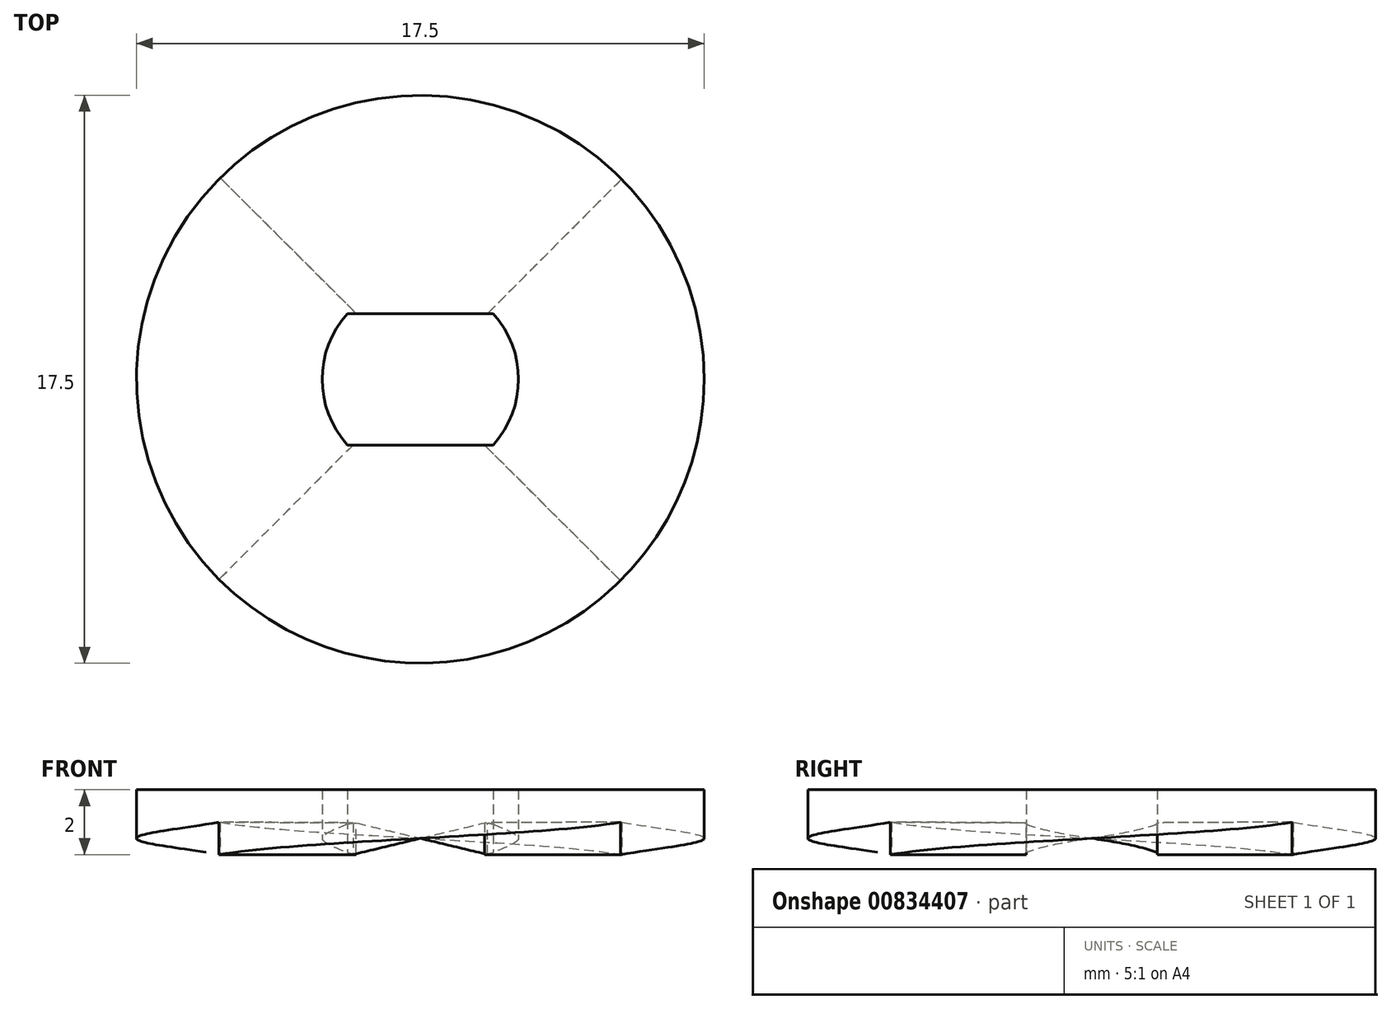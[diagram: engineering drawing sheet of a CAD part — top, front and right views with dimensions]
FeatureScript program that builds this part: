
annotation { "Feature Type Name" : "Feature", "Feature Type Description" : "" }
export const myFeature = defineFeature(function(context is Context, id is Id, definition is map)
    precondition{}
    {
        {
            var Q0;
            Q0=qCreatedBy(makeId("Front.planeOp"),FACE);
            var sketch = newSketch(context, id + "F0", { "sketchPlane" : qUnion([Q0])});
            skLineSegment(sketch, "E0", {"start": v(-0.05, 0) * mm, "end": v(0.05, 1) * mm});
            skLineSegment(sketch, "E1", {"start": v(0.05, 1) * mm, "end": v(0.05, 2) * mm});
            skLineSegment(sketch, "E2", {"start": v(0.05, 2) * mm, "end": v(-0.05, 2) * mm});
            skLineSegment(sketch, "E3", {"start": v(-0.05, 2) * mm, "end": v(-0.05, 0) * mm});
            skLineSegment(sketch, "E4", {"start": v(0, 13.58) * mm, "end": v(0, 25.88) * mm});
            skSolve(sketch);
        }
        {
            var Q0;
            Q0=qCreatedBy(makeId("Front.planeOp"),FACE);
            cPlane(context, id + "F1", {"entities" : qUnion([Q0]), "cplaneType" : CPlaneType.OFFSET, "offset" : 20 * mm, "width" : 150 * mm, "height" : 150 * mm});
        }
        {
            var Q0;
            Q0=qCreatedBy(id+"F1.planeOp",FACE);
            var sketch = newSketch(context, id + "F2", { "sketchPlane" : qUnion([Q0])});
            skLineSegment(sketch, "E5", {"start": v(-20, 0) * mm, "end": v(20, 1) * mm});
            skLineSegment(sketch, "E6", {"start": v(20, 1) * mm, "end": v(20, 2) * mm});
            skLineSegment(sketch, "E7", {"start": v(20, 2) * mm, "end": v(-20, 2) * mm});
            skLineSegment(sketch, "E8", {"start": v(-20, 2) * mm, "end": v(-20, 0) * mm});
            skSolve(sketch);
        }
        {
            var Q0;
            Q0=makeQuery(id+"F0.imprint","IMPRINT",FACE,{"disambiguationData":[TD([[makeQuery(id+"F0.imprint","IMPRINT",EDGE,{"derivedFrom":sQuery(id+"F0.wireOp",EDGE,"E0")}),1.0]])]});
            var Q1;
            Q1=makeQuery(id+"F2.imprint","IMPRINT",FACE,{"disambiguationData":[TD([[makeQuery(id+"F2.imprint","IMPRINT",EDGE,{"derivedFrom":sQuery(id+"F2.wireOp",EDGE,"E5")}),1.0]])]});
            loft(context, id + "F3", {"sheetProfilesArray" : [{ "sheetProfileEntities" : qUnion([Q0]) }, { "sheetProfileEntities" : qUnion([Q1]) }]});
        }
        {
            var Q0;
            Q0=makeQuery(id+"F3.opLoft","SWEPT_BODY",BODY,{"disambiguationData":[OSD([makeQuery(id+"F0.imprint","IMPRINT",FACE,{"disambiguationData":[TD([[makeQuery(id+"F0.imprint","IMPRINT",EDGE,{"derivedFrom":sQuery(id+"F0.wireOp",EDGE,"E0")}),1.0]])]}),makeQuery(id+"F2.imprint","IMPRINT",FACE,{"disambiguationData":[TD([[makeQuery(id+"F2.imprint","IMPRINT",EDGE,{"derivedFrom":sQuery(id+"F2.wireOp",EDGE,"E5")}),1.0]])]})])]});
            var Q1;
            Q1=sQuery(id+"F0.wireOp",EDGE,"E4");
            circularPattern(context, id + "F4", {"operationType" : NewBodyOperationType.ADD, "entities" : qUnion([Q0]), "axis" : qUnion([Q1]), "angle" : 360 * degree, "instanceCount" : 4, "equalSpace" : true});
        }
        {
            var Q0;
            Q0=qCreatedBy(makeId("Top.planeOp"),FACE);
            var sketch = newSketch(context, id + "F5", { "sketchPlane" : qUnion([Q0])});
            skCircle(sketch, "E9", {"center": v(0, 0) * mm, "radius": 8.75 * mm});
            skLineSegment(sketch, "E10.bottom", {"start": v(3.02, 2.02) * mm, "end": v(-3.02, 2.02) * mm});
            skLineSegment(sketch, "E10.top", {"start": v(3.02, -2.02) * mm, "end": v(-3.02, -2.02) * mm});
            skLineSegment(sketch, "E10.left", {"start": v(3.02, 2.02) * mm, "end": v(3.02, -2.02) * mm});
            skLineSegment(sketch, "E10.right", {"start": v(-3.02, 2.02) * mm, "end": v(-3.02, -2.02) * mm});
            skCircle(sketch, "E11", {"center": v(0, 0) * mm, "radius": 3.02 * mm});
            skCircle(sketch, "E12", {"center": v(0, 0) * mm, "radius": 3.02 * mm, "construction": true});
            skSolve(sketch);
        }
        {
            var Q0;
            Q0=makeQuery(id+"F5.imprint","IMPRINT",FACE,{"disambiguationData":[TD([[makeQuery(id+"F5.imprint","IMPRINT",EDGE,{"derivedFrom":sQuery(id+"F5.wireOp",EDGE,"E9")}),1.0]])]});
            var Q1;
            {var subQ0=sQuery(id+"F5.wireOp",EDGE,"E11");var subQ1=sQuery(id+"F5.wireOp",EDGE,"E10.left");var subQ2=makeQuery(id+"F5.imprint","INTERSECT",VERTEX,{"disambiguationData":[OD(0.0)],"derivedFrom":[subQ1,subQ0]});Q1=makeQuery(id+"F5.imprint","IMPRINT",FACE,{"disambiguationData":[TD([[makeQuery(id+"F5.imprint","IMPRINT",EDGE,{"disambiguationData":[TD([[subQ2,-1.0]])],"derivedFrom":subQ1}),1.0]])]});}
            var Q2;
            {var subQ0=sQuery(id+"F5.wireOp",EDGE,"E10.left");var subQ1=sQuery(id+"F5.wireOp",EDGE,"E10.bottom");var subQ2=makeQuery(id+"F5.imprint","INTERSECT",VERTEX,{"derivedFrom":[subQ1,subQ0]});Q2=makeQuery(id+"F5.imprint","IMPRINT",FACE,{"disambiguationData":[TD([[makeQuery(id+"F5.imprint","IMPRINT",EDGE,{"disambiguationData":[TD([[subQ2,-1.0]])],"derivedFrom":subQ1}),1.0]])]});}
            var Q3;
            {var subQ0=sQuery(id+"F5.wireOp",EDGE,"E10.right");var subQ1=sQuery(id+"F5.wireOp",EDGE,"E10.bottom");var subQ2=makeQuery(id+"F5.imprint","INTERSECT",VERTEX,{"derivedFrom":[subQ1,subQ0]});Q3=makeQuery(id+"F5.imprint","IMPRINT",FACE,{"disambiguationData":[TD([[makeQuery(id+"F5.imprint","IMPRINT",EDGE,{"disambiguationData":[TD([[subQ2,1.0]])],"derivedFrom":subQ1}),1.0]])]});}
            var Q4;
            {var subQ0=sQuery(id+"F5.wireOp",EDGE,"E11");var subQ1=sQuery(id+"F5.wireOp",EDGE,"E10.right");var subQ2=makeQuery(id+"F5.imprint","INTERSECT",VERTEX,{"disambiguationData":[OD(0.0)],"derivedFrom":[subQ1,subQ0]});Q4=makeQuery(id+"F5.imprint","IMPRINT",FACE,{"disambiguationData":[TD([[makeQuery(id+"F5.imprint","IMPRINT",EDGE,{"disambiguationData":[TD([[subQ2,-1.0]])],"derivedFrom":subQ1}),-1.0]])]});}
            var Q5;
            {var subQ0=sQuery(id+"F5.wireOp",EDGE,"E10.right");var subQ1=sQuery(id+"F5.wireOp",EDGE,"E10.top");var subQ2=makeQuery(id+"F5.imprint","INTERSECT",VERTEX,{"derivedFrom":[subQ1,subQ0]});Q5=makeQuery(id+"F5.imprint","IMPRINT",FACE,{"disambiguationData":[TD([[makeQuery(id+"F5.imprint","IMPRINT",EDGE,{"disambiguationData":[TD([[subQ2,1.0]])],"derivedFrom":subQ1}),-1.0]])]});}
            var Q6;
            {var subQ0=sQuery(id+"F5.wireOp",EDGE,"E10.left");var subQ1=sQuery(id+"F5.wireOp",EDGE,"E10.top");var subQ2=makeQuery(id+"F5.imprint","INTERSECT",VERTEX,{"derivedFrom":[subQ1,subQ0]});Q6=makeQuery(id+"F5.imprint","IMPRINT",FACE,{"disambiguationData":[TD([[makeQuery(id+"F5.imprint","IMPRINT",EDGE,{"disambiguationData":[TD([[subQ2,-1.0]])],"derivedFrom":subQ1}),-1.0]])]});}
            var Q7;
            {var subQ0=sQuery(id+"F5.wireOp",EDGE,"E11");var subQ1=sQuery(id+"F5.wireOp",EDGE,"E10.top");var subQ2=makeQuery(id+"F5.imprint","INTERSECT",VERTEX,{"disambiguationData":[OD(0.0)],"derivedFrom":[subQ1,subQ0]});Q7=makeQuery(id+"F5.imprint","IMPRINT",FACE,{"disambiguationData":[TD([[makeQuery(id+"F5.imprint","IMPRINT",EDGE,{"disambiguationData":[TD([[subQ2,-1.0]])],"derivedFrom":subQ1}),1.0]])]});}
            var Q8;
            {var subQ0=sQuery(id+"F5.wireOp",EDGE,"E11");var subQ1=sQuery(id+"F5.wireOp",EDGE,"E10.bottom");var subQ2=makeQuery(id+"F5.imprint","INTERSECT",VERTEX,{"disambiguationData":[OD(0.0)],"derivedFrom":[subQ1,subQ0]});Q8=makeQuery(id+"F5.imprint","IMPRINT",FACE,{"disambiguationData":[TD([[makeQuery(id+"F5.imprint","IMPRINT",EDGE,{"disambiguationData":[TD([[subQ2,-1.0]])],"derivedFrom":subQ1}),-1.0]])]});}
            extrude(context, id + "F6", {"entities" : qUnion([Q0, Q1, Q2, Q3, Q4, Q5, Q6, Q7, Q8]), "depth" : 25 * mm, "offsetDistance" : 25 * mm});
        }
        {
            var Q0;
            Q0=makeQuery(id+"F6.opExtrude","SWEPT_BODY",BODY,{"disambiguationData":[OSD([sQuery(id+"F5.wireOp",EDGE,"E9"),sQuery(id+"F5.wireOp",EDGE,"E10.bottom"),sQuery(id+"F5.wireOp",EDGE,"E10.top"),sQuery(id+"F5.wireOp",EDGE,"E10.left"),sQuery(id+"F5.wireOp",EDGE,"E10.right")])]});
            var Q1;
            Q1=makeQuery(id+"F3.opLoft","SWEPT_BODY",BODY,{"disambiguationData":[OSD([makeQuery(id+"F0.imprint","IMPRINT",FACE,{"disambiguationData":[TD([[makeQuery(id+"F0.imprint","IMPRINT",EDGE,{"derivedFrom":sQuery(id+"F0.wireOp",EDGE,"E0")}),1.0]])]}),makeQuery(id+"F2.imprint","IMPRINT",FACE,{"disambiguationData":[TD([[makeQuery(id+"F2.imprint","IMPRINT",EDGE,{"derivedFrom":sQuery(id+"F2.wireOp",EDGE,"E5")}),1.0]])]})])]});
            booleanBodies(context, id + "F7", {"operationType" : BooleanOperationType.INTERSECTION, "tools" : qUnion([Q0, Q1])});
        }
    });
